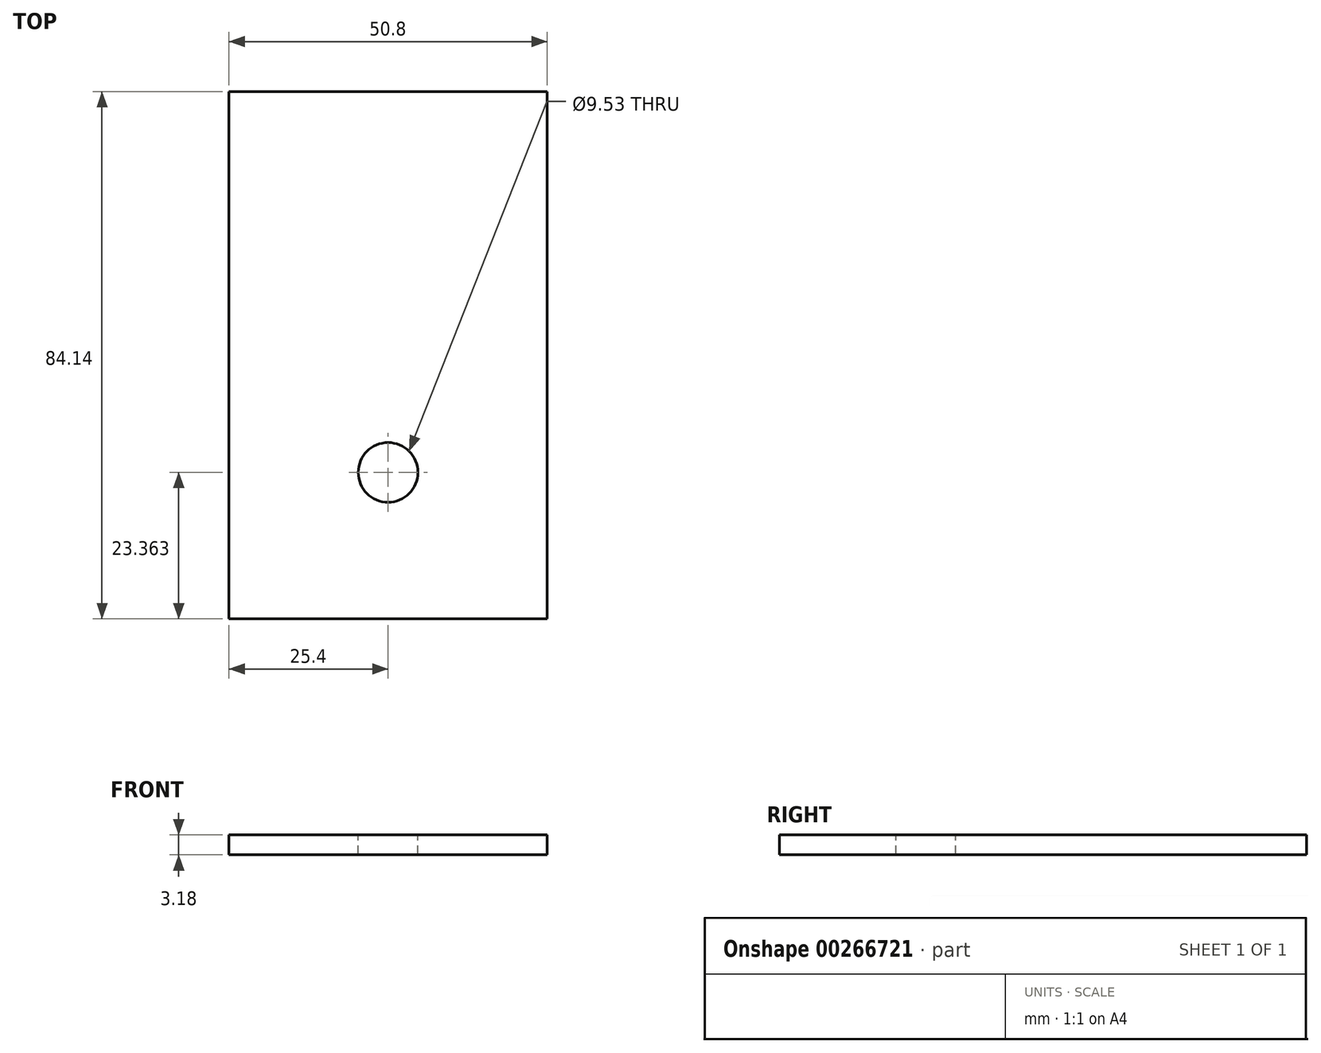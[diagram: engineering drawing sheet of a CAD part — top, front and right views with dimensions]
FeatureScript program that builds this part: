
annotation { "Feature Type Name" : "Feature", "Feature Type Description" : "" }
export const myFeature = defineFeature(function(context is Context, id is Id, definition is map)
    precondition{}
    {
        {
            var Q0;
            Q0=qCreatedBy(makeId("Top.planeOp"),FACE);
            var sketch = newSketch(context, id + "F0", { "sketchPlane" : qUnion([Q0])});
            skLineSegment(sketch, "E0.bottom", {"start": v(-25.4, 42.07) * mm, "end": v(25.4, 42.07) * mm});
            skLineSegment(sketch, "E0.top", {"start": v(-25.4, -42.07) * mm, "end": v(25.4, -42.07) * mm});
            skLineSegment(sketch, "E0.left", {"start": v(-25.4, 42.07) * mm, "end": v(-25.4, -42.07) * mm});
            skLineSegment(sketch, "E0.right", {"start": v(25.4, 42.07) * mm, "end": v(25.4, -42.07) * mm});
            skPoint(sketch, "E0.middle", {"position": v(0, 0) * mm});
            skSolve(sketch);
        }
        {
            var Q0;
            Q0 = qSketchRegion(id + "F0", true);
            var Q1;
            Q1=makeQuery(id+"F0.imprint","IMPRINT",FACE,{"disambiguationData":[TD([[makeQuery(id+"F0.imprint","IMPRINT",EDGE,{"derivedFrom":sQuery(id+"F0.wireOp",EDGE,"E0.bottom")}),-1.0]])]});
            extrude(context, id + "F1", {"entities" : qUnion([Q0, Q1]), "depth" : 3.17 * mm});
        }
        {
            var Q0;
            Q0=makeQuery(id+"F1.opExtrude","CAP_FACE",FACE,{"disambiguationData":[OSD([sQuery(id+"F0.wireOp",EDGE,"E0.bottom"),sQuery(id+"F0.wireOp",EDGE,"E0.top"),sQuery(id+"F0.wireOp",EDGE,"E0.left"),sQuery(id+"F0.wireOp",EDGE,"E0.right")])],"isStart":false});
            var sketch = newSketch(context, id + "F2", { "sketchPlane" : qUnion([Q0])});
            skPoint(sketch, "E1", {"position": v(0, -18.7) * mm});
            skSolve(sketch);
        }
        {
            var Q0;
            Q0=sQuery(id+"F2.wireOp",VERTEX,"E1");
            var Q1;
            Q1=makeQuery(id+"F1.opExtrude","SWEPT_BODY",BODY,{"disambiguationData":[OSD([sQuery(id+"F0.wireOp",EDGE,"E0.bottom"),sQuery(id+"F0.wireOp",EDGE,"E0.top"),sQuery(id+"F0.wireOp",EDGE,"E0.left"),sQuery(id+"F0.wireOp",EDGE,"E0.right")])]});
            hole(context, id + "F3", {"style" : HoleStyle.SIMPLE, "endStyle" : HoleEndStyle.THROUGH, "holeDiameter" : 9.52 * mm, "tappedDepth" : 12.7 * mm, "tapClearance" : 3, "locations" : qUnion([Q0]), "scope" : qUnion([Q1])});
        }
    });
